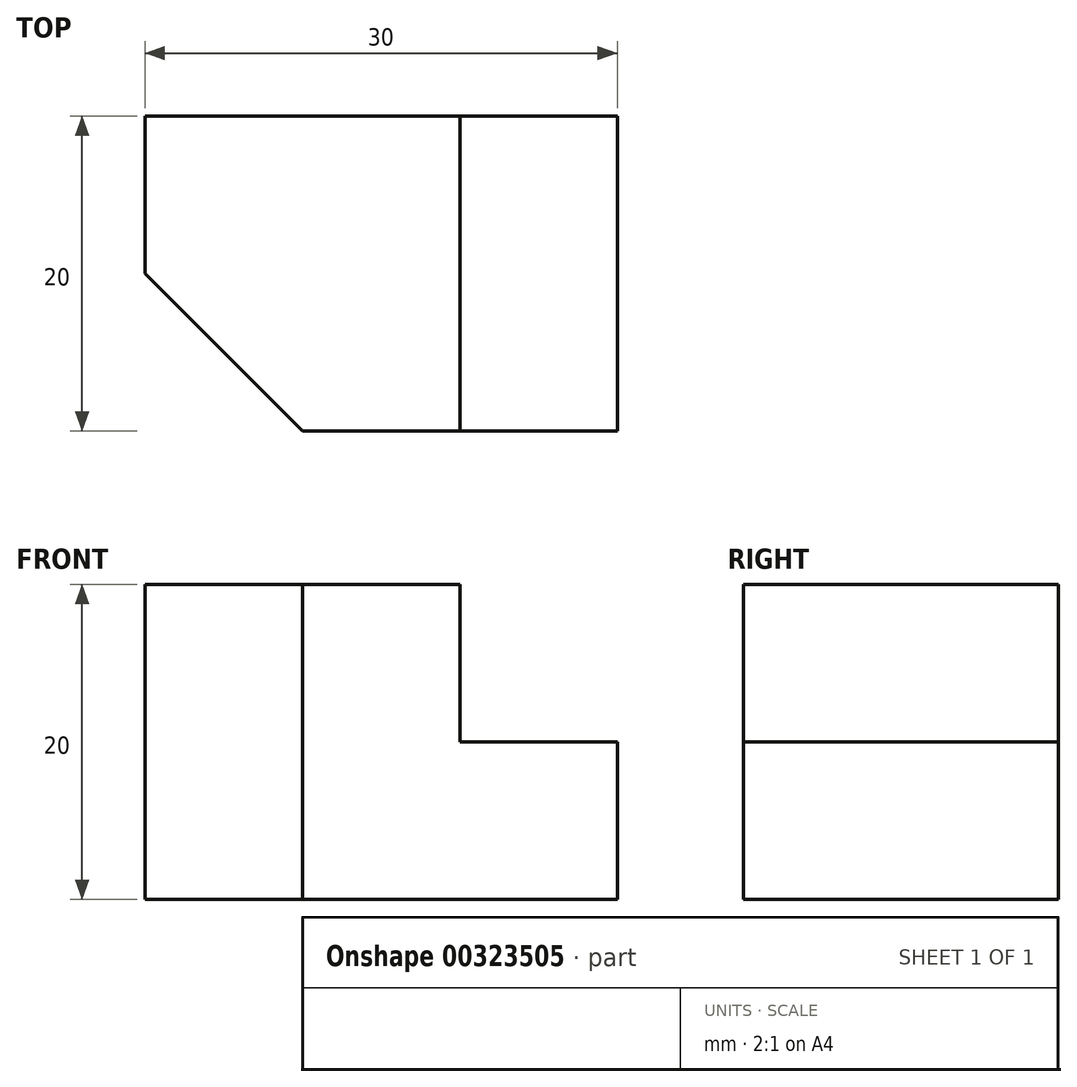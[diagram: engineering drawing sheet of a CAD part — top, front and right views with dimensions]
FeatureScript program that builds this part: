
annotation { "Feature Type Name" : "Feature", "Feature Type Description" : "" }
export const myFeature = defineFeature(function(context is Context, id is Id, definition is map)
    precondition{}
    {
        {
            var Q0;
            Q0=qCreatedBy(makeId("Front.planeOp"),FACE);
            var sketch = newSketch(context, id + "F0", { "sketchPlane" : qUnion([Q0])});
            skLineSegment(sketch, "E0.bottom", {"start": v(-15, 20) * mm, "end": v(15, 20) * mm});
            skLineSegment(sketch, "E0.top", {"start": v(-15, 0) * mm, "end": v(15, 0) * mm});
            skLineSegment(sketch, "E0.left", {"start": v(-15, 20) * mm, "end": v(-15, 0) * mm});
            skLineSegment(sketch, "E0.right", {"start": v(15, 20) * mm, "end": v(15, 0) * mm});
            skSolve(sketch);
        }
        {
            var Q0;
            Q0=makeQuery(id+"F0.imprint","IMPRINT",FACE,{"disambiguationData":[TD([[makeQuery(id+"F0.imprint","IMPRINT",EDGE,{"derivedFrom":sQuery(id+"F0.wireOp",EDGE,"E0.bottom")}),-1.0]])]});
            extrude(context, id + "F1", {"entities" : qUnion([Q0]), "endBound" : BoundingType.SYMMETRIC, "depth" : 20 * mm});
        }
        {
            var Q0;
            Q0=makeQuery(id+"F1.opExtrude","CAP_FACE",FACE,{"disambiguationData":[OSD([sQuery(id+"F0.wireOp",EDGE,"E0.bottom"),sQuery(id+"F0.wireOp",EDGE,"E0.top"),sQuery(id+"F0.wireOp",EDGE,"E0.left"),sQuery(id+"F0.wireOp",EDGE,"E0.right")])],"isStart":false});
            var sketch = newSketch(context, id + "F2", { "sketchPlane" : qUnion([Q0])});
            skLineSegment(sketch, "E1.0.2", {"start": v(15, 10) * mm, "end": v(15, 20) * mm});
            skLineSegment(sketch, "E1.0.3", {"start": v(15, 20) * mm, "end": v(5, 20) * mm});
            skPoint(sketch, "E2.oppositeSnap0", {"position": v(15, 10) * mm});
            skLineSegment(sketch, "E2.top", {"start": v(15, 10) * mm, "end": v(5, 10) * mm});
            skLineSegment(sketch, "E2.left", {"start": v(15, 20) * mm, "end": v(15, 10) * mm});
            skLineSegment(sketch, "E2.right", {"start": v(5, 20) * mm, "end": v(5, 10) * mm});
            skPoint(sketch, "E1.0.0.start.orphan", {"position": v(-15, 20) * mm});
            skPoint(sketch, "E1.0.1.start.orphan", {"position": v(-15, 0) * mm});
            skPoint(sketch, "E3.orphan", {"position": v(15, 0) * mm});
            skSolve(sketch);
        }
        {
            var Q0;
            Q0 = qSketchRegion(id + "F2", true);
            extrude(context, id + "F3", {"entities" : qUnion([Q0]), "operationType" : NewBodyOperationType.REMOVE, "endBound" : BoundingType.THROUGH_ALL, "oppositeDirection" : true, "depth" : 25 * mm});
        }
        {
            var Q0;
            Q0=makeQuery(id+"F1.opExtrude","SWEPT_FACE",FACE,{"disambiguationData":[OSD([sQuery(id+"F0.wireOp",EDGE,"E0.bottom")])]});
            var sketch = newSketch(context, id + "F4", { "sketchPlane" : qUnion([Q0])});
            skLineSegment(sketch, "E4", {"start": v(-15, 0) * mm, "end": v(-5, -10) * mm});
            skLineSegment(sketch, "E5", {"start": v(-5, -10) * mm, "end": v(-15, -10) * mm});
            skLineSegment(sketch, "E6", {"start": v(-15, -10) * mm, "end": v(-15, 0) * mm});
            skSolve(sketch);
        }
        {
            var Q0;
            Q0 = qSketchRegion(id + "F4", true);
            extrude(context, id + "F5", {"entities" : qUnion([Q0]), "operationType" : NewBodyOperationType.REMOVE, "endBound" : BoundingType.THROUGH_ALL, "oppositeDirection" : true, "depth" : 25 * mm});
        }
    });
